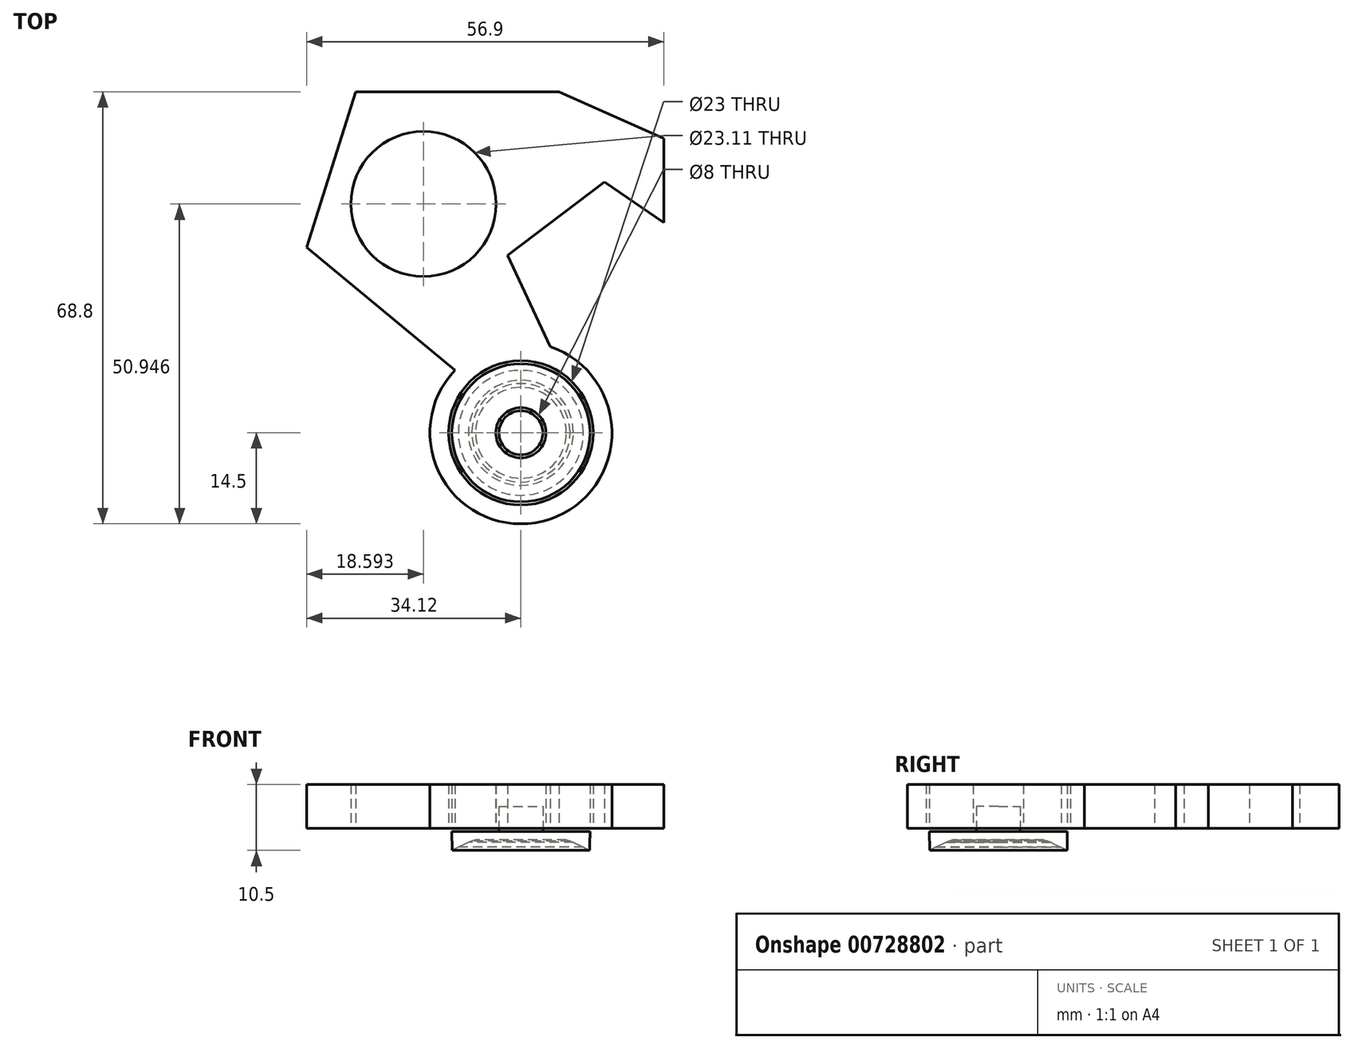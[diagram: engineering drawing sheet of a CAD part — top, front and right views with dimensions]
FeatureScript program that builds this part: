
annotation { "Feature Type Name" : "Feature", "Feature Type Description" : "" }
export const myFeature = defineFeature(function(context is Context, id is Id, definition is map)
    precondition{}
    {
        {
            var Q0;
            Q0=qCreatedBy(makeId("Top.planeOp"),FACE);
            var sketch = newSketch(context, id + "F0", { "sketchPlane" : qUnion([Q0])});
            skCircle(sketch, "E0", {"center": v(0, 0) * mm, "radius": 11 * mm});
            skCircle(sketch, "E1", {"center": v(0, 0) * mm, "radius": 4 * mm});
            skSolve(sketch);
        }
        {
            var Q0;
            Q0 = qSketchRegion(id + "F0", true);
            extrude(context, id + "F1", {"entities" : qUnion([Q0]), "depth" : 7 * mm, "offsetDistance" : 25 * mm});
        }
        {
            var Q0;
            Q0=qCreatedBy(makeId("Top.planeOp"),FACE);
            var sketch = newSketch(context, id + "F2", { "sketchPlane" : qUnion([Q0])});
            skCircle(sketch, "E2", {"center": v(0, 0) * mm, "radius": 11.5 * mm});
            skLineSegment(sketch, "E3", {"start": v(6.8, 9.28) * mm, "end": v(-2.14, 28.26) * mm});
            skLineSegment(sketch, "E4", {"start": v(-2.14, 28.26) * mm, "end": v(13.3, 39.98) * mm});
            skLineSegment(sketch, "E5", {"start": v(13.3, 39.98) * mm, "end": v(22.78, 33.47) * mm});
            skLineSegment(sketch, "E6", {"start": v(22.78, 33.47) * mm, "end": v(22.78, 46.86) * mm});
            skLineSegment(sketch, "E7", {"start": v(22.78, 46.86) * mm, "end": v(6.04, 54.3) * mm});
            skLineSegment(sketch, "E8", {"start": v(6.04, 54.3) * mm, "end": v(-26.31, 54.3) * mm});
            skLineSegment(sketch, "E9", {"start": v(-26.31, 54.3) * mm, "end": v(-34.12, 29.57) * mm});
            skLineSegment(sketch, "E10", {"start": v(-34.12, 29.57) * mm, "end": v(-8.18, 8.08) * mm});
            skCircle(sketch, "E11", {"center": v(0, 0) * mm, "radius": 3.5 * mm});
            skCircle(sketch, "E12", {"center": v(-15.53, 36.45) * mm, "radius": 11.55 * mm});
            skSolve(sketch);
        }
        {
            var Q0;
            Q0=qCreatedBy(makeId("Top.planeOp"),FACE);
            var sketch = newSketch(context, id + "F3", { "sketchPlane" : qUnion([Q0])});
            skCircle(sketch, "E13", {"center": v(0, 0) * mm, "radius": 11.5 * mm});
            skCircle(sketch, "E14", {"center": v(0, 0) * mm, "radius": 14.5 * mm});
            skSolve(sketch);
        }
        {
            var Q0;
            Q0=makeQuery(id+"F3.imprint","IMPRINT",FACE,{"disambiguationData":[TD([[makeQuery(id+"F3.imprint","IMPRINT",EDGE,{"derivedFrom":sQuery(id+"F3.wireOp",EDGE,"E13")}),-1.0]])]});
            extrude(context, id + "F4", {"entities" : qUnion([Q0]), "depth" : 7 * mm, "offsetDistance" : 25 * mm});
        }
        {
            var Q0;
            {var subQ0=sQuery(id+"F2.wireOp",EDGE,"E3");Q0=makeQuery(id+"F2.imprint","IMPRINT",FACE,{"disambiguationData":[TD([[makeQuery(id+"F2.imprint","IMPRINT",EDGE,{"derivedFrom":subQ0}),1.0]])]});}
            extrude(context, id + "F5", {"entities" : qUnion([Q0]), "operationType" : NewBodyOperationType.ADD, "depth" : 7 * mm, "offsetDistance" : 25 * mm});
        }
        {
            var Q0;
            Q0=qCreatedBy(makeId("Top.planeOp"),FACE);
            var sketch = newSketch(context, id + "F6", { "sketchPlane" : qUnion([Q0])});
            skCircle(sketch, "E15", {"center": v(0, 0) * mm, "radius": 3.5 * mm});
            skSolve(sketch);
        }
        {
            var Q0;
            Q0 = qSketchRegion(id + "F6", true);
            extrude(context, id + "F7", {"entities" : qUnion([Q0]), "depth" : 3.5 * mm, "offsetDistance" : 25 * mm});
        }
        {
            var Q0;
            Q0=makeQuery(id+"F7.opExtrude","CAP_FACE",FACE,{"disambiguationData":[OSD([sQuery(id+"F6.wireOp",EDGE,"E15")])],"isStart":true});
            extrude(context, id + "F8", {"entities" : qUnion([Q0]), "operationType" : NewBodyOperationType.ADD, "depth" : 1 * mm, "offsetDistance" : 25 * mm});
        }
        {
            var Q0;
            Q0=qCreatedBy(makeId("Right.planeOp"),FACE);
            var sketch = newSketch(context, id + "F9", { "sketchPlane" : qUnion([Q0])});
            skLineSegment(sketch, "E16", {"start": v(11, -0.5) * mm, "end": v(0, -0.5) * mm});
            skLineSegment(sketch, "E17", {"start": v(0, -0.5) * mm, "end": v(0, -1.83) * mm});
            skLineSegment(sketch, "E18", {"start": v(0, -1.83) * mm, "end": v(7.24, -1.83) * mm});
            skLineSegment(sketch, "E19", {"start": v(7.24, -1.83) * mm, "end": v(7.83, -2) * mm});
            skLineSegment(sketch, "E20", {"start": v(7.83, -2) * mm, "end": v(8.36, -2.23) * mm});
            skLineSegment(sketch, "E21", {"start": v(8.36, -2.23) * mm, "end": v(8.96, -2.5) * mm});
            skLineSegment(sketch, "E22", {"start": v(8.96, -2.5) * mm, "end": v(9.96, -3) * mm});
            skLineSegment(sketch, "E23", {"start": v(9.96, -3) * mm, "end": v(10.97, -3.5) * mm});
            skLineSegment(sketch, "E24", {"start": v(10.97, -3.5) * mm, "end": v(11, -0.5) * mm});
            skSolve(sketch);
        }
        {
            var Q0;
            Q0 = qSketchRegion(id + "F9", true);
            var Q1;
            Q1=sQuery(id+"F9.wireOp",EDGE,"E17");
            revolve(context, id + "F10", {"operationType" : NewBodyOperationType.ADD, "surfaceOperationType" : NewSurfaceOperationType.NEW, "entities" : qUnion([Q0]), "axis" : qUnion([Q1]), "revolveType" : RevolveType.FULL});
        }
    });
